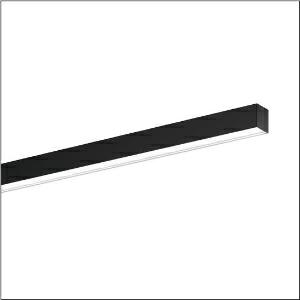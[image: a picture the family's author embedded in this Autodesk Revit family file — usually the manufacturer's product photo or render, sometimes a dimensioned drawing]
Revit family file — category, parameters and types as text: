
# Revit family: silica_r__21_51mx20dc35bb_a1de
name_source: partatom
category: Lighting Fixtures
units: mm (PartAtom-declared; Revit-internal decimal feet)

## family parameters
Cut with Voids When Loaded = No
Host = Face
Light Source = No
Part Type = Normal
Room Calculation Point = No
Round Connector Dimension = Use Diameter
Shared = No

## types (1)
- --- (1 x LED, 6000 lm, 42.6 W, 3000K)
    Apparent Load = 43 VA
    CIE Flux Codes = 48 79 96 100 100
    Color Rendering = 80
    Color Temperature = 3000K
    Default Elevation = 1800 mm
    Description = Silica® 21, office luminaire, primary optical cover: cover, of PMMA, opal, light emission: direct distribution, primary light characteristic: symmetric, installation type: surface-mounted, LED, rated luminous flux: 6.000lm, luminous efficacy: 141lm/W, light colour: 830, colour temperature: 3000K, with terminal, 3+2-pole, max. 2.5mm², mains connection: 220..240V, AC, 50/60Hz, rated input power: 42.6W, luminaire housing, of aluminium, jet black (RAL 9005), length: 3.004mm, width: 53mm, height: 53mm, protection rating (complete): IP20, insulation class (complete): insulation class I (protective earthing), certification: CE, permissible operating ambient temperature: 0..+35°C, standard: EN 50419, packaging unit: 1 piece
    Height = 0 mm  [stored 0 ft]
    Lamp = 1 x LED
    Lamp Light Flux = 6000 lm
    Lamp Power = 42.6 W
    Lamp count = 1
    Length = 3004 mm
    Luminous efficacy = 141 lm/W
    Manufacturer = Siteco
    ModVariant = No
    Model = 51MX20DC35BB
    Mounting Place = Ceiling
    Mounting Type = Recessed
    Number of Poles = 1
    OnlyDefault = Yes
    Power Factor = 1
    Product Name = Silica® 21
    Product group = office luminaire | ceiling recessed
    ProductGroupID = 401
    Protection Class = Protection class I
    Protection Degree = IP 20
    RLX_Detail_Level = 1
    RLX_Emergency_Light_Flux = 0 lm
    RLX_Emergency_Type = 0
    RLX_Emergency_Type_DB = No
    RlxData = <blob elided: 28977 chars, md5=37466bde>
    Socket = socket
    Standby Power = 0 W
    System Light Flux = 6000 lm
    System Power = 43 W
    Type Comments = factory setting: luminous flux: 100 % | dim-lin: 254 | 233 mA
    Type Image = l_1297760.jpg
    URL = http://relux.com
    VarID = @adj_047921
    Voltage = 0 V
    Weight = 0.00 kg
    Width = 53 mm

note: [stored X ft] marks values corroborated as IEEE doubles in the binary element streams (Revit-internal decimal feet)

## geometry (parser evidence)
native form markers: Blend x4, Sweep x10
no freeform markers — native parametric forms only
